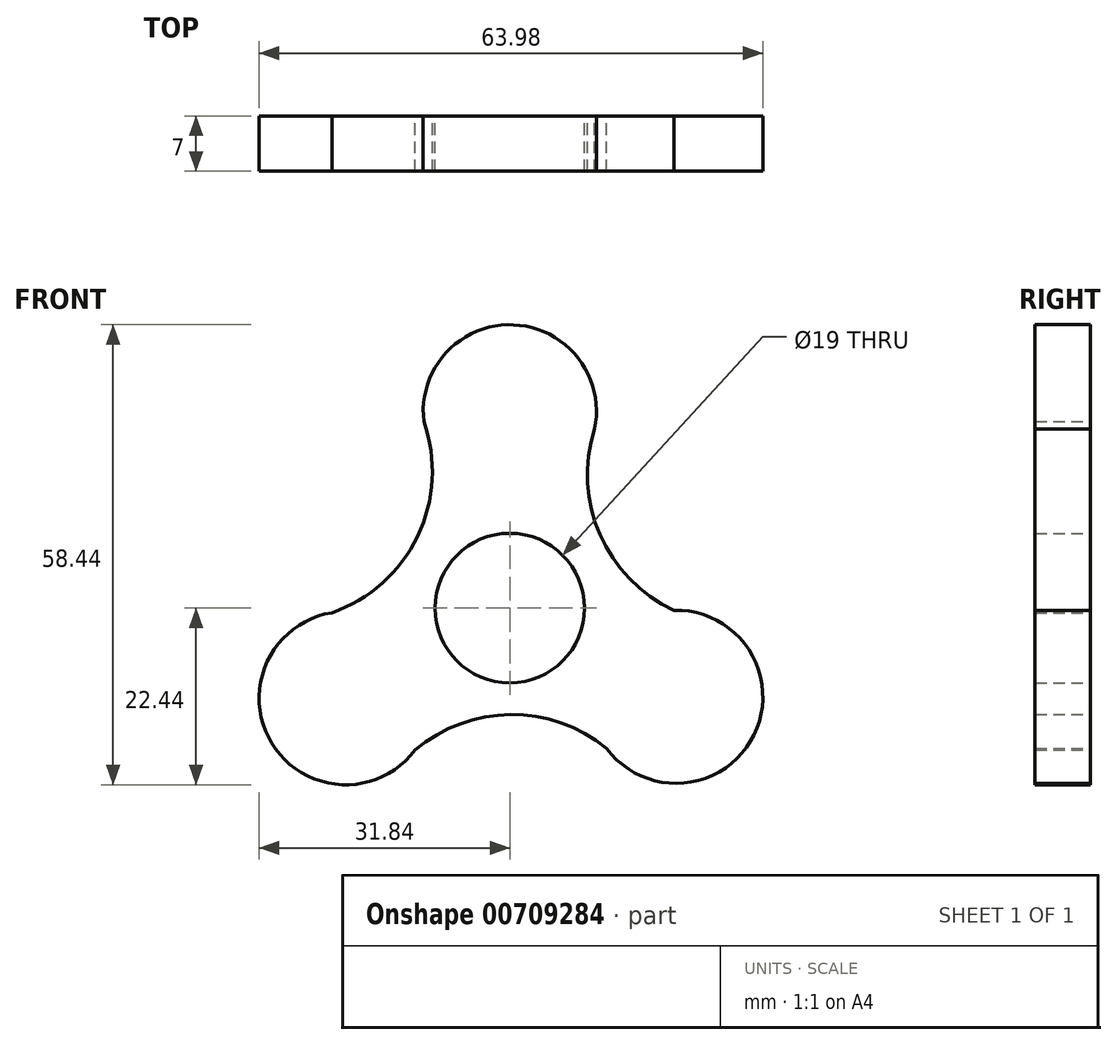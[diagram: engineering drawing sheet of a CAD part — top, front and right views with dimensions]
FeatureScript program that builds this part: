
annotation { "Feature Type Name" : "Feature", "Feature Type Description" : "" }
export const myFeature = defineFeature(function(context is Context, id is Id, definition is map)
    precondition{}
    {
        {
            var Q0;
            Q0=qCreatedBy(makeId("Front.planeOp"),FACE);
            var sketch = newSketch(context, id + "F0", { "sketchPlane" : qUnion([Q0])});
            skCircle(sketch, "E0", {"center": v(0, 0) * mm, "radius": 9.5 * mm});
            skArc(sketch, "E1", {"start": v(10.38, 21.35) * mm, "mid": v(-0.33, 36) * mm, "end": v(-10.14, 20.74) * mm});
            skArc(sketch, "E2.1.0", {"start": v(-22.6, -0.58) * mm, "mid": v(-30.25, -17.14) * mm, "end": v(-12.03, -18.02) * mm});
            skArc(sketch, "E2.2.0", {"start": v(12.3, -17.82) * mm, "mid": v(31.03, -16.09) * mm, "end": v(20.85, -0.27) * mm});
            skPoint(sketch, "E2.center", {"position": v(0.1, 0.76) * mm});
            skArc(sketch, "E3", {"start": v(-22.6, -0.58) * mm, "mid": v(-11.72, 9.12) * mm, "end": v(-10.92, 23.69) * mm});
            skArc(sketch, "E4", {"start": v(12.3, -17.82) * mm, "mid": v(0.1, -13.53) * mm, "end": v(-12.03, -18.02) * mm});
            skArc(sketch, "E5", {"start": v(10.77, 22.76) * mm, "mid": v(11.46, 9.34) * mm, "end": v(20.85, -0.27) * mm});
            skSolve(sketch);
        }
        {
            var Q0;
            Q0=makeQuery(id+"F0.imprint","IMPRINT",FACE,{"disambiguationData":[TD([[makeQuery(id+"F0.imprint","IMPRINT",EDGE,{"derivedFrom":sQuery(id+"F0.wireOp",EDGE,"E0")}),-1.0]])]});
            extrude(context, id + "F1", {"entities" : qUnion([Q0]), "depth" : 7 * mm, "offsetDistance" : 25 * mm});
        }
    });
